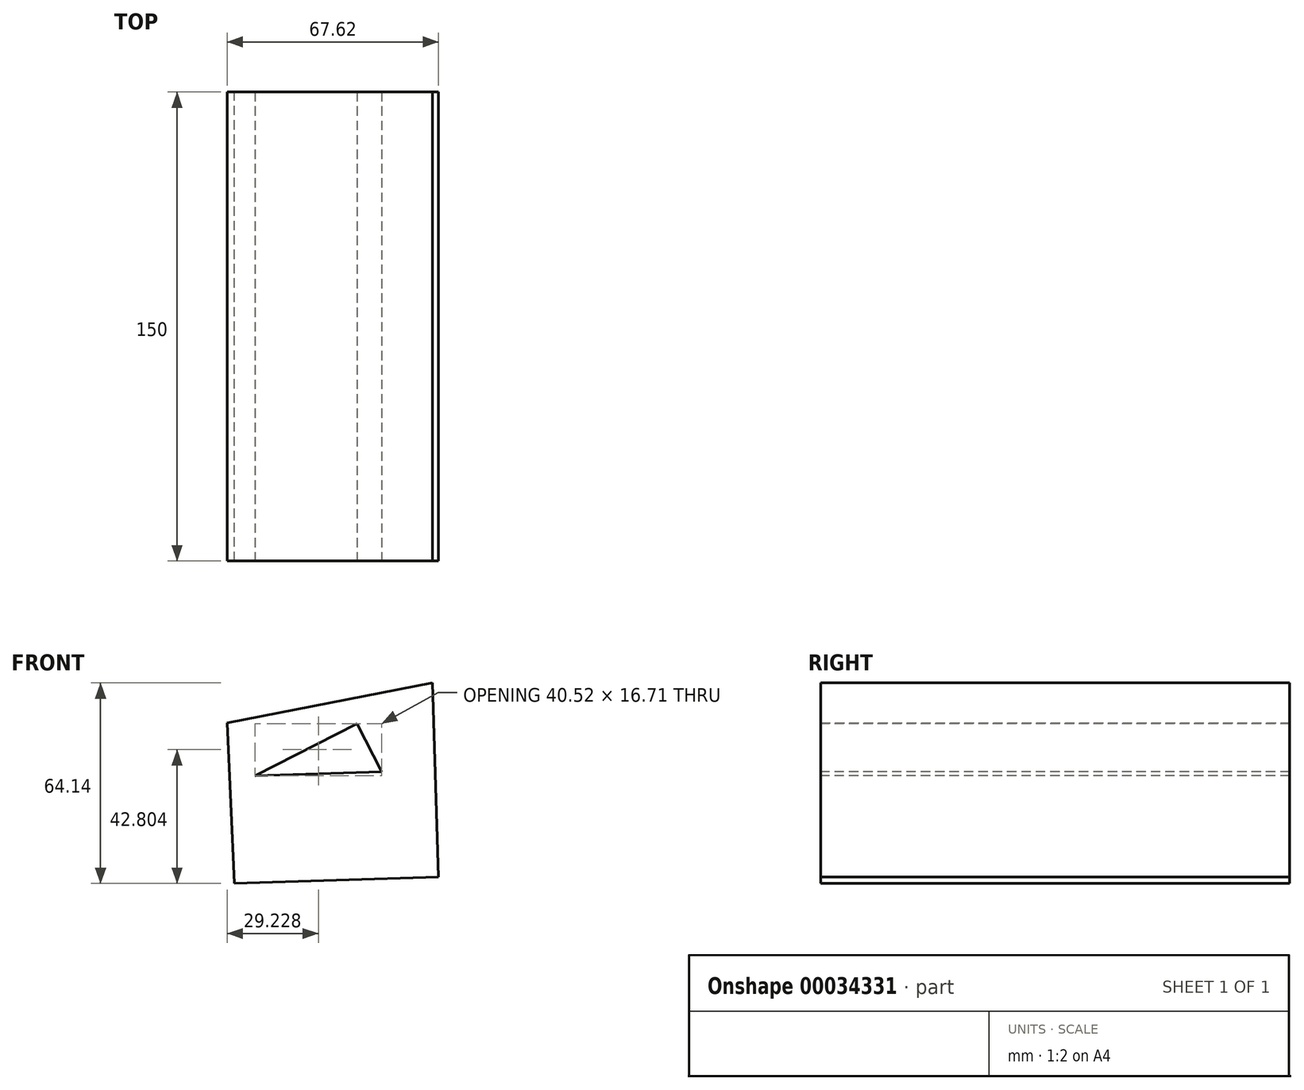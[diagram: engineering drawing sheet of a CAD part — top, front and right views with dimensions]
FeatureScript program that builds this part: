
annotation { "Feature Type Name" : "Feature", "Feature Type Description" : "" }
export const myFeature = defineFeature(function(context is Context, id is Id, definition is map)
    precondition{}
    {
        {
            var Q0;
            Q0=qCreatedBy(makeId("Front.planeOp"),FACE);
            var sketch = newSketch(context, id + "F0", { "sketchPlane" : qUnion([Q0])});
            skLineSegment(sketch, "E0", {"start": v(-37.4, 29.6) * mm, "end": v(28.28, 42.41) * mm});
            skLineSegment(sketch, "E1", {"start": v(28.28, 42.41) * mm, "end": v(30.22, -19.68) * mm});
            skLineSegment(sketch, "E2", {"start": v(30.22, -19.68) * mm, "end": v(-35.1, -21.73) * mm});
            skLineSegment(sketch, "E3", {"start": v(-35.1, -21.73) * mm, "end": v(-37.4, 29.6) * mm});
            skSolve(sketch);
        }
        {
            var Q0;
            Q0=makeQuery(id+"F0.imprint","IMPRINT",FACE,{"disambiguationData":[TD([[makeQuery(id+"F0.imprint","IMPRINT",EDGE,{"derivedFrom":sQuery(id+"F0.wireOp",EDGE,"E0")}),-1.0]])]});
            extrude(context, id + "F1", {"entities" : qUnion([Q0]), "depth" : 150 * mm});
        }
        {
            var Q0;
            Q0=makeQuery(id+"F1.opExtrude","CAP_FACE",FACE,{"disambiguationData":[OSD([sQuery(id+"F0.wireOp",EDGE,"E0"),sQuery(id+"F0.wireOp",EDGE,"E1"),sQuery(id+"F0.wireOp",EDGE,"E2"),sQuery(id+"F0.wireOp",EDGE,"E3")])],"isStart":false});
            var sketch = newSketch(context, id + "F2", { "sketchPlane" : qUnion([Q0])});
            skLineSegment(sketch, "E4", {"start": v(-28.43, 12.72) * mm, "end": v(4.17, 29.43) * mm});
            skLineSegment(sketch, "E5", {"start": v(4.17, 29.43) * mm, "end": v(12.09, 13.99) * mm});
            skLineSegment(sketch, "E6", {"start": v(12.09, 13.99) * mm, "end": v(-28.43, 12.72) * mm});
            skSolve(sketch);
        }
        {
            var Q0;
            Q0=makeQuery(id+"F2.imprint","IMPRINT",FACE,{"disambiguationData":[TD([[makeQuery(id+"F2.imprint","IMPRINT",EDGE,{"derivedFrom":sQuery(id+"F2.wireOp",EDGE,"E4")}),-1.0]])]});
            var Q1;
            Q1=makeQuery(id+"F1.opExtrude","CAP_FACE",FACE,{"disambiguationData":[OSD([sQuery(id+"F0.wireOp",EDGE,"E0"),sQuery(id+"F0.wireOp",EDGE,"E1"),sQuery(id+"F0.wireOp",EDGE,"E2"),sQuery(id+"F0.wireOp",EDGE,"E3")])],"isStart":true});
            extrude(context, id + "F3", {"entities" : qUnion([Q0]), "operationType" : NewBodyOperationType.REMOVE, "endBound" : BoundingType.UP_TO_SURFACE, "oppositeDirection" : true, "endBoundEntityFace" : qUnion([Q1]), "depth" : 95.74 * mm});
        }
    });
